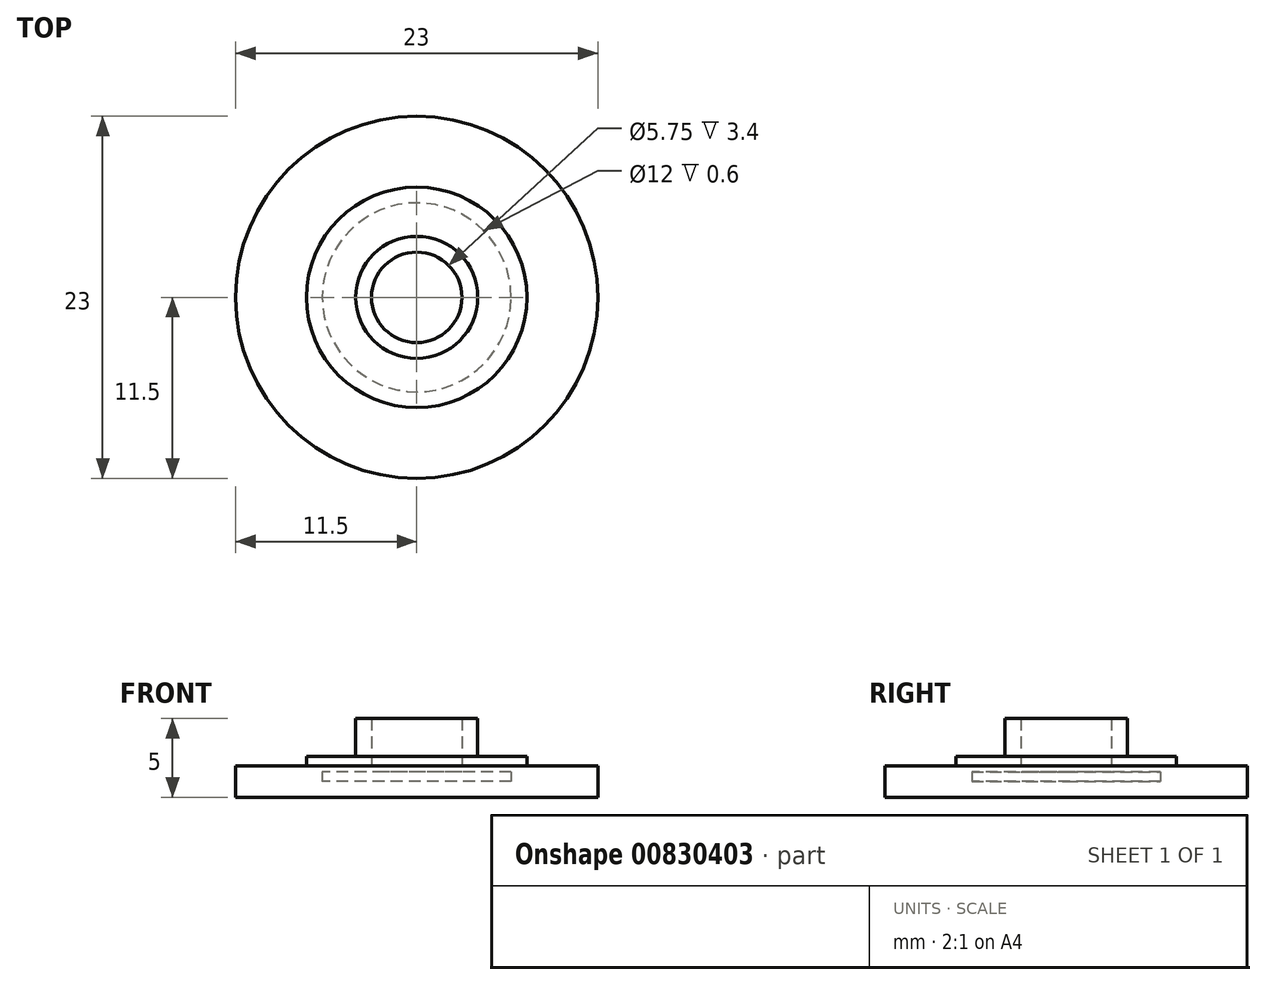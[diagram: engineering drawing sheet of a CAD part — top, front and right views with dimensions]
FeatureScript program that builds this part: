
annotation { "Feature Type Name" : "Feature", "Feature Type Description" : "" }
export const myFeature = defineFeature(function(context is Context, id is Id, definition is map)
    precondition{}
    {
        {
            var Q0;
            Q0=qCreatedBy(makeId("Top.planeOp"),FACE);
            var sketch = newSketch(context, id + "F0", { "sketchPlane" : qUnion([Q0])});
            skCircle(sketch, "E0", {"center": v(0, 0) * mm, "radius": 3.88 * mm});
            skCircle(sketch, "E1", {"center": v(0, 0) * mm, "radius": 7 * mm});
            skCircle(sketch, "E2", {"center": v(0, 0) * mm, "radius": 11.5 * mm});
            skSolve(sketch);
        }
        {
            var Q0;
            Q0=makeQuery(id+"F0.imprint","IMPRINT",FACE,{"disambiguationData":[TD([[makeQuery(id+"F0.imprint","IMPRINT",EDGE,{"derivedFrom":sQuery(id+"F0.wireOp",EDGE,"E0")}),1.0]])]});
            extrude(context, id + "F1", {"entities" : qUnion([Q0]), "depth" : 3 * mm, "offsetDistance" : 25 * mm});
        }
        {
            var Q0;
            Q0=makeQuery(id+"F0.imprint","IMPRINT",FACE,{"disambiguationData":[TD([[makeQuery(id+"F0.imprint","IMPRINT",EDGE,{"derivedFrom":sQuery(id+"F0.wireOp",EDGE,"E0")}),-1.0]])]});
            extrude(context, id + "F2", {"entities" : qUnion([Q0]), "operationType" : NewBodyOperationType.ADD, "depth" : 0.6 * mm, "offsetDistance" : 25 * mm});
        }
        {
            var Q0;
            Q0=makeQuery(id+"F0.imprint","IMPRINT",FACE,{"disambiguationData":[TD([[makeQuery(id+"F0.imprint","IMPRINT",EDGE,{"derivedFrom":sQuery(id+"F0.wireOp",EDGE,"E0")}),-1.0]])]});
            var Q1;
            Q1=makeQuery(id+"F0.imprint","IMPRINT",FACE,{"disambiguationData":[TD([[makeQuery(id+"F0.imprint","IMPRINT",EDGE,{"derivedFrom":sQuery(id+"F0.wireOp",EDGE,"E1")}),-1.0]])]});
            extrude(context, id + "F3", {"entities" : qUnion([Q0, Q1]), "operationType" : NewBodyOperationType.ADD, "oppositeDirection" : true, "depth" : 2 * mm, "offsetDistance" : 25 * mm});
        }
        {
            var Q0;
            Q0=makeQuery(id+"F0.imprint","IMPRINT",FACE,{"disambiguationData":[TD([[makeQuery(id+"F0.imprint","IMPRINT",EDGE,{"derivedFrom":sQuery(id+"F0.wireOp",EDGE,"E0")}),1.0]])]});
            extrude(context, id + "F4", {"entities" : qUnion([Q0]), "operationType" : NewBodyOperationType.ADD, "oppositeDirection" : true, "depth" : 2 * mm, "offsetDistance" : 25 * mm});
        }
        {
            var Q0;
            Q0=sQuery(id+"F0.wireOp",EDGE,"E0");
            extrude(context, id + "F5", {"bodyType" : ToolBodyType.SURFACE, "surfaceEntities" : qUnion([Q0]), "depth" : 3.4 * mm, "offsetDistance" : 25 * mm});
        }
        {
            var Q0;
            Q0=makeQuery(id+"F1.opExtrude","CAP_FACE",FACE,{"disambiguationData":[OSD([sQuery(id+"F0.wireOp",EDGE,"E0")])],"isStart":false});
            shell(context, id + "F6", {"entities" : qUnion([Q0]), "thickness" : 1 * mm});
        }
    });
